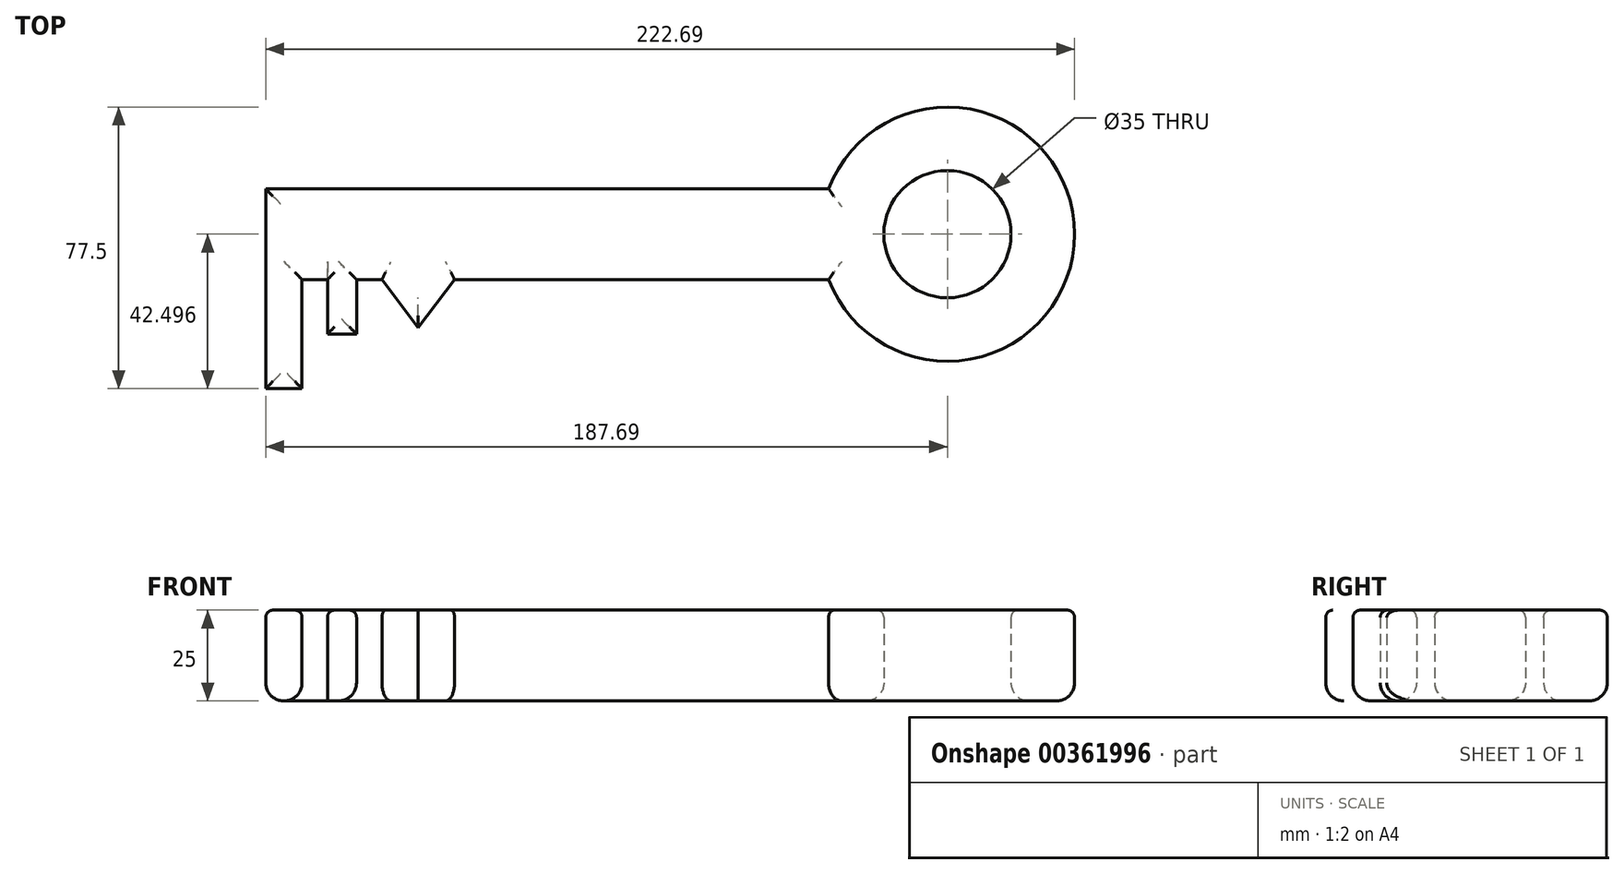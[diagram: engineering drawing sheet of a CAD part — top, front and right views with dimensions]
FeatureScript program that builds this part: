
annotation { "Feature Type Name" : "Feature", "Feature Type Description" : "" }
export const myFeature = defineFeature(function(context is Context, id is Id, definition is map)
    precondition{}
    {
        {
            var Q0;
            Q0=qCreatedBy(makeId("Top.planeOp"),FACE);
            var sketch = newSketch(context, id + "F0", { "sketchPlane" : qUnion([Q0])});
            skLineSegment(sketch, "E0.bottom", {"start": v(-68.96, 2.06) * mm, "end": v(86.04, 2.06) * mm});
            skLineSegment(sketch, "E0.top", {"start": v(-68.96, -22.94) * mm, "end": v(86.04, -22.94) * mm});
            skLineSegment(sketch, "E0.left", {"start": v(-68.96, 2.06) * mm, "end": v(-68.96, -22.94) * mm});
            skLineSegment(sketch, "E0.right", {"start": v(86.04, -22.94) * mm, "end": v(86.04, -22.94) * mm});
            skCircle(sketch, "E1", {"center": v(118.73, -10.44) * mm, "radius": 17.5 * mm});
            skArc(sketch, "E2", {"start": v(86.04, -22.94) * mm, "mid": v(153.73, -10.44) * mm, "end": v(86.04, 2.06) * mm});
            skLineSegment(sketch, "E3", {"start": v(-36.96, -22.94) * mm, "end": v(-26.96, -36.13) * mm});
            skLineSegment(sketch, "E4", {"start": v(-26.96, -36.13) * mm, "end": v(-16.96, -22.94) * mm});
            skLineSegment(sketch, "E5", {"start": v(-68.96, -22.94) * mm, "end": v(-68.96, -52.94) * mm});
            skLineSegment(sketch, "E6", {"start": v(-68.96, -52.94) * mm, "end": v(-58.96, -52.94) * mm});
            skLineSegment(sketch, "E7", {"start": v(-58.96, -52.94) * mm, "end": v(-58.96, -22.94) * mm});
            skLineSegment(sketch, "E8", {"start": v(-51.96, -22.94) * mm, "end": v(-51.96, -37.94) * mm});
            skLineSegment(sketch, "E9", {"start": v(-51.96, -37.94) * mm, "end": v(-43.96, -37.94) * mm});
            skLineSegment(sketch, "E10", {"start": v(-43.96, -37.94) * mm, "end": v(-43.96, -22.94) * mm});
            skSolve(sketch);
        }
        {
            var Q0;
            Q0=makeQuery(id+"F0.imprint","IMPRINT",FACE,{"disambiguationData":[TD([[makeQuery(id+"F0.imprint","IMPRINT",EDGE,{"derivedFrom":sQuery(id+"F0.wireOp",EDGE,"E0.bottom")}),-1.0]])]});
            var Q1;
            {var subQ0=sQuery(id+"F0.wireOp",EDGE,"E5");Q1=makeQuery(id+"F0.imprint","IMPRINT",FACE,{"disambiguationData":[TD([[makeQuery(id+"F0.imprint","IMPRINT",EDGE,{"derivedFrom":subQ0}),1.0]])]});}
            var Q2;
            {var subQ0=sQuery(id+"F0.wireOp",EDGE,"E8");Q2=makeQuery(id+"F0.imprint","IMPRINT",FACE,{"disambiguationData":[TD([[makeQuery(id+"F0.imprint","IMPRINT",EDGE,{"derivedFrom":subQ0}),1.0]])]});}
            var Q3;
            {var subQ0=sQuery(id+"F0.wireOp",EDGE,"E3");Q3=makeQuery(id+"F0.imprint","IMPRINT",FACE,{"disambiguationData":[TD([[makeQuery(id+"F0.imprint","IMPRINT",EDGE,{"derivedFrom":subQ0}),1.0]])]});}
            extrude(context, id + "F1", {"entities" : qUnion([Q0, Q1, Q2, Q3]), "depth" : 25 * mm});
        }
        {
            var Q0;
            Q0=makeQuery(id+"F1.opExtrude","CAP_EDGE",EDGE,{"disambiguationData":[OSD([sQuery(id+"F0.wireOp",EDGE,"E0.bottom")])],"isStart":false});
            var Q1;
            {var subQ0=sQuery(id+"F0.wireOp",EDGE,"E0.top");Q1=makeQuery(id+"F1.opExtrude","CAP_EDGE",EDGE,{"disambiguationData":[OSD([subQ0]),TDD([makeQuery(id+"F0.imprint","IMPRINT",EDGE,{"disambiguationData":[TD([[makeQuery(id+"F0.imprint","INTERSECT",VERTEX,{"derivedFrom":[subQ0,sQuery(id+"F0.wireOp",EDGE,"E2")]}),1.0]])],"derivedFrom":subQ0})])],"isStart":false});}
            var Q2;
            Q2=makeQuery(id+"F1.opExtrude","CAP_EDGE",EDGE,{"disambiguationData":[OSD([sQuery(id+"F0.wireOp",EDGE,"E4")])],"isStart":false});
            var Q3;
            Q3=makeQuery(id+"F1.opExtrude","CAP_EDGE",EDGE,{"disambiguationData":[OSD([sQuery(id+"F0.wireOp",EDGE,"E3")])],"isStart":false});
            var Q4;
            {var subQ0=sQuery(id+"F0.wireOp",EDGE,"E0.top");Q4=makeQuery(id+"F1.opExtrude","CAP_EDGE",EDGE,{"disambiguationData":[OSD([subQ0]),TDD([makeQuery(id+"F0.imprint","IMPRINT",EDGE,{"disambiguationData":[TD([[makeQuery(id+"F0.imprint","INTERSECT",VERTEX,{"derivedFrom":[subQ0,sQuery(id+"F0.wireOp",EDGE,"E3")]}),1.0]])],"derivedFrom":subQ0})])],"isStart":false});}
            var Q5;
            Q5=makeQuery(id+"F1.opExtrude","CAP_EDGE",EDGE,{"disambiguationData":[OSD([sQuery(id+"F0.wireOp",EDGE,"E10")])],"isStart":false});
            var Q6;
            Q6=makeQuery(id+"F1.opExtrude","CAP_EDGE",EDGE,{"disambiguationData":[OSD([sQuery(id+"F0.wireOp",EDGE,"E9")])],"isStart":false});
            var Q7;
            {var subQ0=sQuery(id+"F0.wireOp",EDGE,"E0.top");Q7=makeQuery(id+"F1.opExtrude","CAP_EDGE",EDGE,{"disambiguationData":[OSD([subQ0]),TDD([makeQuery(id+"F0.imprint","IMPRINT",EDGE,{"disambiguationData":[TD([[makeQuery(id+"F0.imprint","INTERSECT",VERTEX,{"derivedFrom":[subQ0,sQuery(id+"F0.wireOp",EDGE,"E7")]}),-1.0]])],"derivedFrom":subQ0})])],"isStart":false});}
            var Q8;
            Q8=makeQuery(id+"F1.opExtrude","CAP_EDGE",EDGE,{"disambiguationData":[OSD([sQuery(id+"F0.wireOp",EDGE,"E8")])],"isStart":false});
            var Q9;
            Q9=makeQuery(id+"F1.opExtrude","CAP_EDGE",EDGE,{"disambiguationData":[OSD([sQuery(id+"F0.wireOp",EDGE,"E7")])],"isStart":false});
            var Q10;
            Q10=makeQuery(id+"F1.opExtrude","CAP_EDGE",EDGE,{"disambiguationData":[OSD([sQuery(id+"F0.wireOp",EDGE,"E6")])],"isStart":false});
            var Q11;
            Q11=makeQuery(id+"F1.opExtrude","CAP_EDGE",EDGE,{"disambiguationData":[OSD([sQuery(id+"F0.wireOp",EDGE,"E0.left"),sQuery(id+"F0.wireOp",EDGE,"E5")])],"isStart":false});
            var Q12;
            Q12=makeQuery(id+"F1.opExtrude","CAP_EDGE",EDGE,{"disambiguationData":[OSD([sQuery(id+"F0.wireOp",EDGE,"E2")])],"isStart":false});
            var Q13;
            Q13=makeQuery(id+"F1.opExtrude","CAP_EDGE",EDGE,{"disambiguationData":[OSD([sQuery(id+"F0.wireOp",EDGE,"E1")])],"isStart":false});
            fillet(context, id + "F2", {"entities" : qUnion([Q0, Q1, Q2, Q3, Q4, Q5, Q6, Q7, Q8, Q9, Q10, Q11, Q12, Q13]), "radius" : 2 * mm, "tangentPropagation" : true, "allowEdgeOverflow" : false});
        }
        {
            var Q0;
            Q0=makeQuery(id+"F1.opExtrude","CAP_EDGE",EDGE,{"disambiguationData":[OSD([sQuery(id+"F0.wireOp",EDGE,"E4")])],"isStart":true});
            var Q1;
            Q1=makeQuery(id+"F1.opExtrude","CAP_EDGE",EDGE,{"disambiguationData":[OSD([sQuery(id+"F0.wireOp",EDGE,"E3")])],"isStart":true});
            var Q2;
            {var subQ0=sQuery(id+"F0.wireOp",EDGE,"E0.top");Q2=makeQuery(id+"F1.opExtrude","CAP_EDGE",EDGE,{"disambiguationData":[OSD([subQ0]),TDD([makeQuery(id+"F0.imprint","IMPRINT",EDGE,{"disambiguationData":[TD([[makeQuery(id+"F0.imprint","INTERSECT",VERTEX,{"derivedFrom":[subQ0,sQuery(id+"F0.wireOp",EDGE,"E2")]}),1.0]])],"derivedFrom":subQ0})])],"isStart":true});}
            var Q3;
            Q3=makeQuery(id+"F1.opExtrude","CAP_EDGE",EDGE,{"disambiguationData":[OSD([sQuery(id+"F0.wireOp",EDGE,"E0.bottom")])],"isStart":true});
            var Q4;
            Q4=makeQuery(id+"F1.opExtrude","CAP_EDGE",EDGE,{"disambiguationData":[OSD([sQuery(id+"F0.wireOp",EDGE,"E10")])],"isStart":true});
            var Q5;
            Q5=makeQuery(id+"F1.opExtrude","CAP_EDGE",EDGE,{"disambiguationData":[OSD([sQuery(id+"F0.wireOp",EDGE,"E9")])],"isStart":true});
            var Q6;
            {var subQ0=sQuery(id+"F0.wireOp",EDGE,"E0.top");Q6=makeQuery(id+"F1.opExtrude","CAP_EDGE",EDGE,{"disambiguationData":[OSD([subQ0]),TDD([makeQuery(id+"F0.imprint","IMPRINT",EDGE,{"disambiguationData":[TD([[makeQuery(id+"F0.imprint","INTERSECT",VERTEX,{"derivedFrom":[subQ0,sQuery(id+"F0.wireOp",EDGE,"E3")]}),1.0]])],"derivedFrom":subQ0})])],"isStart":true});}
            var Q7;
            {var subQ0=sQuery(id+"F0.wireOp",EDGE,"E0.top");Q7=makeQuery(id+"F1.opExtrude","CAP_EDGE",EDGE,{"disambiguationData":[OSD([subQ0]),TDD([makeQuery(id+"F0.imprint","IMPRINT",EDGE,{"disambiguationData":[TD([[makeQuery(id+"F0.imprint","INTERSECT",VERTEX,{"derivedFrom":[subQ0,sQuery(id+"F0.wireOp",EDGE,"E7")]}),-1.0]])],"derivedFrom":subQ0})])],"isStart":true});}
            var Q8;
            Q8=makeQuery(id+"F1.opExtrude","CAP_EDGE",EDGE,{"disambiguationData":[OSD([sQuery(id+"F0.wireOp",EDGE,"E7")])],"isStart":true});
            var Q9;
            Q9=makeQuery(id+"F1.opExtrude","CAP_EDGE",EDGE,{"disambiguationData":[OSD([sQuery(id+"F0.wireOp",EDGE,"E0.left"),sQuery(id+"F0.wireOp",EDGE,"E5")])],"isStart":true});
            var Q10;
            Q10=makeQuery(id+"F1.opExtrude","CAP_EDGE",EDGE,{"disambiguationData":[OSD([sQuery(id+"F0.wireOp",EDGE,"E6")])],"isStart":true});
            var Q11;
            Q11=makeQuery(id+"F1.opExtrude","CAP_EDGE",EDGE,{"disambiguationData":[OSD([sQuery(id+"F0.wireOp",EDGE,"E2")])],"isStart":true});
            var Q12;
            Q12=makeQuery(id+"F1.opExtrude","CAP_EDGE",EDGE,{"disambiguationData":[OSD([sQuery(id+"F0.wireOp",EDGE,"E1")])],"isStart":true});
            fillet(context, id + "F3", {"entities" : qUnion([Q0, Q1, Q2, Q3, Q4, Q5, Q6, Q7, Q8, Q9, Q10, Q11, Q12]), "radius" : 5 * mm, "tangentPropagation" : true, "allowEdgeOverflow" : false});
        }
    });
